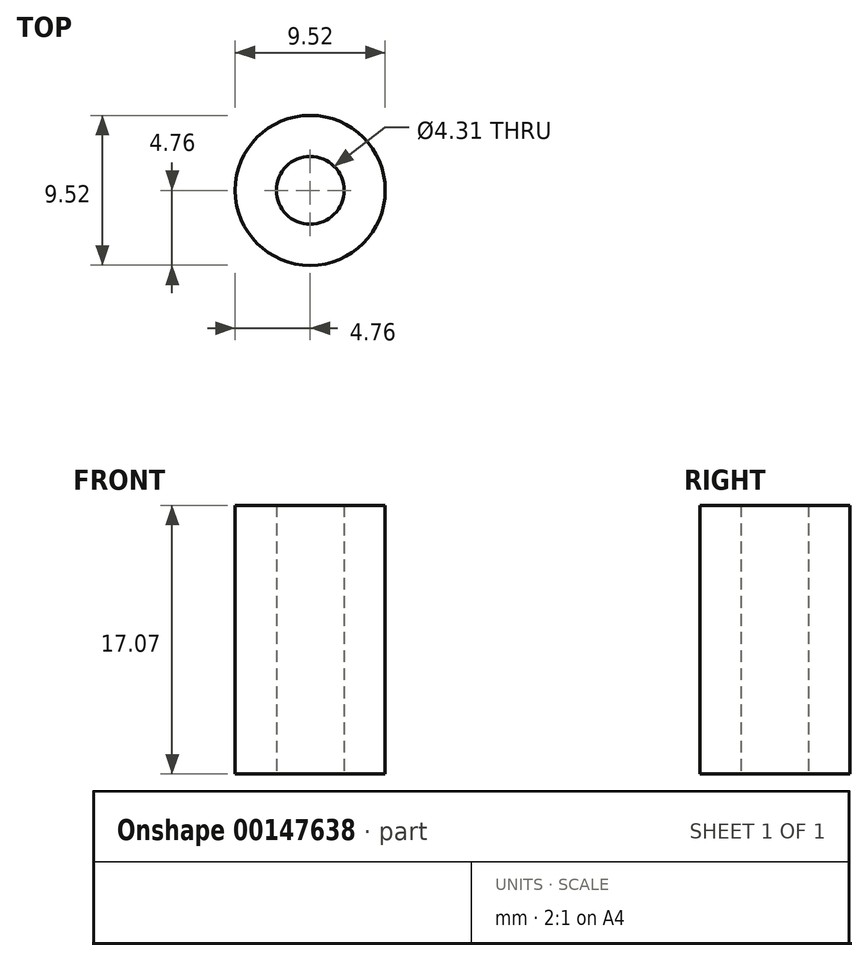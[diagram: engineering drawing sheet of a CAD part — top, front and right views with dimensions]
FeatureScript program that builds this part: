
annotation { "Feature Type Name" : "Feature", "Feature Type Description" : "" }
export const myFeature = defineFeature(function(context is Context, id is Id, definition is map)
    precondition{}
    {
        {
            var Q0;
            Q0=qCreatedBy(makeId("Top.planeOp"),FACE);
            var sketch = newSketch(context, id + "F0", { "sketchPlane" : qUnion([Q0])});
            skCircle(sketch, "E0", {"center": v(0, 0) * mm, "radius": 4.76 * mm});
            skCircle(sketch, "E1", {"center": v(0, 0) * mm, "radius": 2.15 * mm});
            skSolve(sketch);
        }
        {
            var Q0;
            Q0=qSketchRegion(id+"F0",true);
            extrude(context, id + "F1", {"entities" : qUnion([Q0]), "depth" : 17.07 * mm});
        }
    });
